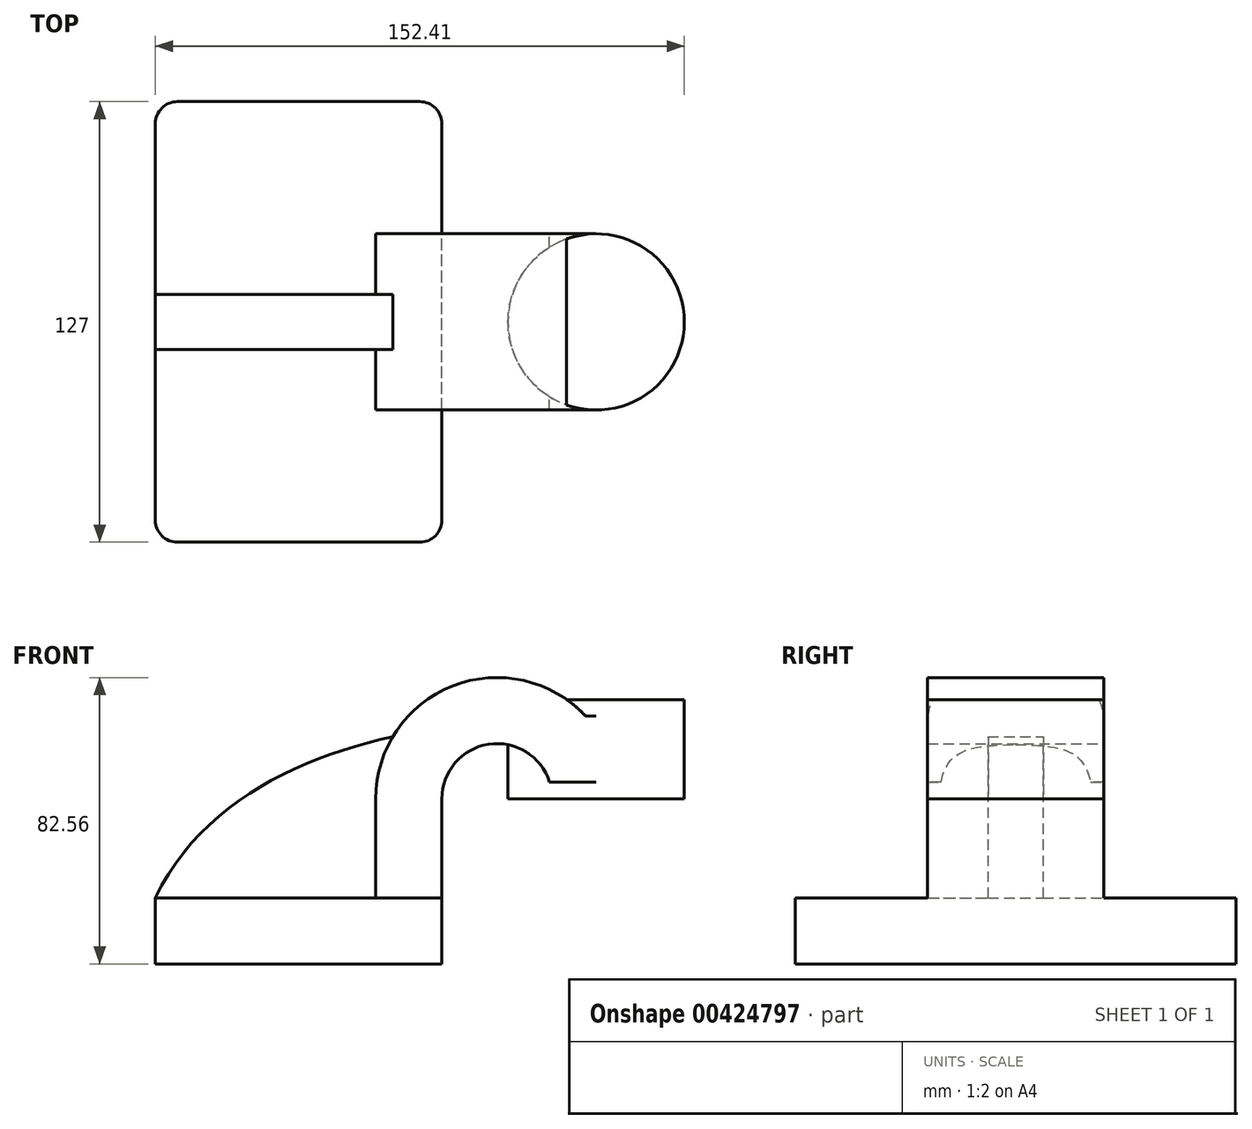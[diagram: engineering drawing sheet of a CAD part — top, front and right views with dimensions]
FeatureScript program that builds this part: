
annotation { "Feature Type Name" : "Feature", "Feature Type Description" : "" }
export const myFeature = defineFeature(function(context is Context, id is Id, definition is map)
    precondition{}
    {
        {
            var Q0;
            Q0=qCreatedBy(makeId("Front.planeOp"),FACE);
            var sketch = newSketch(context, id + "F0", { "sketchPlane" : qUnion([Q0])});
            skLineSegment(sketch, "E0.bottom", {"start": v(41.28, -9.52) * mm, "end": v(-41.28, -9.53) * mm});
            skLineSegment(sketch, "E0.top", {"start": v(41.28, 9.53) * mm, "end": v(-41.28, 9.53) * mm});
            skLineSegment(sketch, "E0.left", {"start": v(41.28, -9.52) * mm, "end": v(41.28, 9.53) * mm});
            skLineSegment(sketch, "E0.right", {"start": v(-41.28, -9.52) * mm, "end": v(-41.28, 9.53) * mm});
            skPoint(sketch, "E0.middle", {"position": v(0, 0) * mm});
            skLineSegment(sketch, "E1.bottom", {"start": v(111.12, 38.1) * mm, "end": v(60.33, 38.1) * mm});
            skLineSegment(sketch, "E1.top", {"start": v(111.12, 66.68) * mm, "end": v(60.33, 66.68) * mm});
            skLineSegment(sketch, "E1.left", {"start": v(111.12, 38.1) * mm, "end": v(111.12, 66.68) * mm});
            skLineSegment(sketch, "E1.right", {"start": v(60.33, 38.1) * mm, "end": v(60.33, 66.68) * mm});
            skPoint(sketch, "E1.middle", {"position": v(85.72, 52.39) * mm});
            skLineSegment(sketch, "E2", {"start": v(41.28, 9.53) * mm, "end": v(41.28, 38.1) * mm});
            skArc(sketch, "E3", {"start": v(41.27, 38.1) * mm, "mid": v(54.73, 53.8) * mm, "end": v(72.29, 42.88) * mm});
            skLineSegment(sketch, "E4", {"start": v(72.29, 42.88) * mm, "end": v(104.26, 42.88) * mm});
            skLineSegment(sketch, "E5.0", {"start": v(82.69, 61.93) * mm, "end": v(104.26, 61.93) * mm});
            skArc(sketch, "E5.1", {"start": v(22.23, 38.1) * mm, "mid": v(44.35, 70.6) * mm, "end": v(82.69, 61.93) * mm});
            skLineSegment(sketch, "E5.2", {"start": v(22.23, 9.53) * mm, "end": v(22.23, 38.1) * mm});
            skLineSegment(sketch, "E6", {"start": v(85.72, 38.1) * mm, "end": v(85.72, 66.68) * mm});
            skFitSpline(sketch, "E7", {"points": [v(-41.28, 9.53) * mm, v(82.69, 61.93) * mm], "startDerivative": vector(67.18, 139.4) * mm, "endDerivative": vector(110.8, 2.27) * mm});
            skSolve(sketch);
        }
        {
            var Q0;
            Q0=makeQuery(id+"F0.imprint","IMPRINT",FACE,{"disambiguationData":[TD([[makeQuery(id+"F0.imprint","IMPRINT",EDGE,{"derivedFrom":sQuery(id+"F0.wireOp",EDGE,"E0.bottom")}),-1.0]])]});
            extrude(context, id + "F1", {"entities" : qUnion([Q0]), "endBound" : BoundingType.SYMMETRIC, "depth" : 127 * mm});
        }
        {
            var Q0;
            {var subQ1=sQuery(id+"F0.wireOp",EDGE,"E2");Q0=makeQuery(id+"F0.imprint","IMPRINT",FACE,{"disambiguationData":[TD([[makeQuery(id+"F0.imprint","IMPRINT",EDGE,{"derivedFrom":subQ1}),1.0]])]});}
            var Q1;
            {var subQ0=sQuery(id+"F0.wireOp",EDGE,"E1.right");var subQ1=sQuery(id+"F0.wireOp",EDGE,"E1.top");var subQ2=makeQuery(id+"F0.imprint","INTERSECT",VERTEX,{"derivedFrom":[subQ1,subQ0]});Q1=makeQuery(id+"F0.imprint","IMPRINT",FACE,{"disambiguationData":[TD([[makeQuery(id+"F0.imprint","IMPRINT",EDGE,{"disambiguationData":[TD([[subQ2,1.0]])],"derivedFrom":subQ1}),-1.0]])]});}
            var Q2;
            {var subQ6=sQuery(id+"F0.wireOp",EDGE,"E3");var subQ8=sQuery(id+"F0.wireOp",EDGE,"E1.right");var subQ9=makeQuery(id+"F0.imprint","INTERSECT",VERTEX,{"derivedFrom":[subQ8,subQ6]});Q2=makeQuery(id+"F0.imprint","IMPRINT",FACE,{"disambiguationData":[TD([[makeQuery(id+"F0.imprint","IMPRINT",EDGE,{"disambiguationData":[TD([[subQ9,-1.0]])],"derivedFrom":subQ8}),-1.0]])]});}
            var Q3;
            {var subQ0=sQuery(id+"F0.wireOp",EDGE,"E1.right");var subQ1=sQuery(id+"F0.wireOp",EDGE,"E1.top");var subQ2=makeQuery(id+"F0.imprint","INTERSECT",VERTEX,{"derivedFrom":[subQ1,subQ0]});Q3=makeQuery(id+"F0.imprint","IMPRINT",FACE,{"disambiguationData":[TD([[makeQuery(id+"F0.imprint","IMPRINT",EDGE,{"disambiguationData":[TD([[subQ2,1.0]])],"derivedFrom":subQ1}),1.0]])]});}
            extrude(context, id + "F2", {"entities" : qUnion([Q0, Q1, Q2, Q3]), "operationType" : NewBodyOperationType.ADD, "endBound" : BoundingType.SYMMETRIC, "depth" : 50.8 * mm});
        }
        {
            var Q0;
            {var subQ3=sQuery(id+"F0.wireOp",EDGE,"E5.2");Q0=makeQuery(id+"F0.imprint","IMPRINT",FACE,{"disambiguationData":[TD([[makeQuery(id+"F0.imprint","IMPRINT",EDGE,{"derivedFrom":subQ3}),1.0]])]});}
            extrude(context, id + "F3", {"entities" : qUnion([Q0]), "operationType" : NewBodyOperationType.ADD, "endBound" : BoundingType.SYMMETRIC, "depth" : 15.88 * mm});
        }
        {
            var Q0;
            {var subQ4=sQuery(id+"F0.wireOp",EDGE,"E1.left");Q0=makeQuery(id+"F0.imprint","IMPRINT",FACE,{"disambiguationData":[TD([[makeQuery(id+"F0.imprint","IMPRINT",EDGE,{"derivedFrom":subQ4}),1.0]])]});}
            var Q1;
            Q1=sQuery(id+"F0.wireOp",EDGE,"E6");
            revolve(context, id + "F4", {"operationType" : NewBodyOperationType.ADD, "entities" : qUnion([Q0]), "axis" : qUnion([Q1]), "revolveType" : RevolveType.FULL});
        }
        {
            var Q0;
            Q0=makeQuery(id+"F1.opExtrude","CAP_EDGE",EDGE,{"disambiguationData":[OSD([sQuery(id+"F0.wireOp",EDGE,"E0.left")])],"isStart":false});
            var Q1;
            Q1=makeQuery(id+"F1.opExtrude","CAP_EDGE",EDGE,{"disambiguationData":[OSD([sQuery(id+"F0.wireOp",EDGE,"E0.left")])],"isStart":true});
            var Q2;
            Q2=makeQuery(id+"F1.opExtrude","CAP_EDGE",EDGE,{"disambiguationData":[OSD([sQuery(id+"F0.wireOp",EDGE,"E0.right")])],"isStart":true});
            var Q3;
            Q3=makeQuery(id+"F1.opExtrude","CAP_EDGE",EDGE,{"disambiguationData":[OSD([sQuery(id+"F0.wireOp",EDGE,"E0.right")])],"isStart":false});
            fillet(context, id + "F5", {"entities" : qUnion([Q0, Q1, Q2, Q3]), "radius" : 6.35 * mm, "tangentPropagation" : true, "allowEdgeOverflow" : false});
        }
    });
